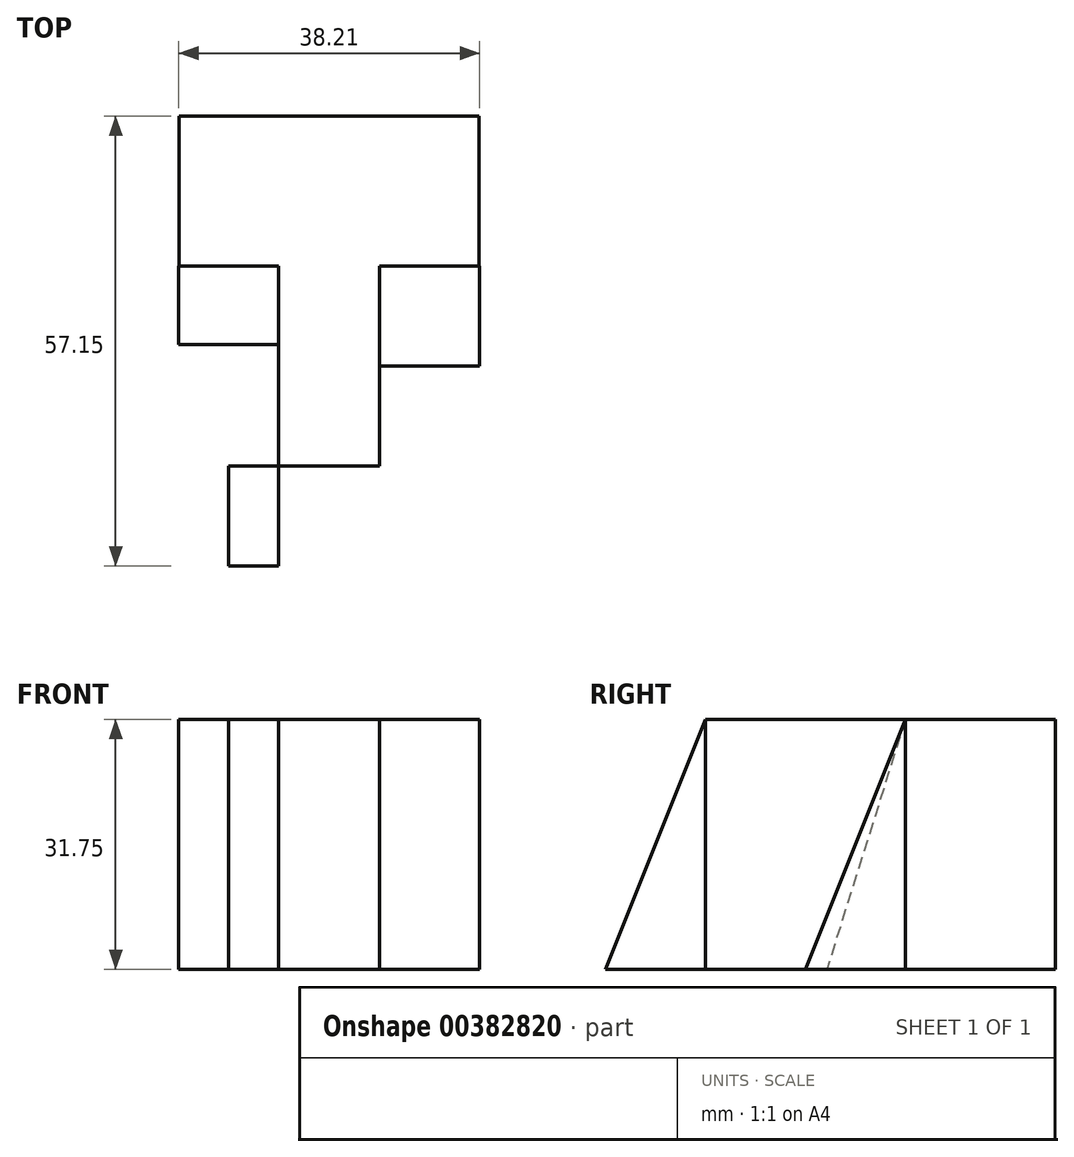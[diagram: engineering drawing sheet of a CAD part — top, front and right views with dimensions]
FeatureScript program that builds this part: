
annotation { "Feature Type Name" : "Feature", "Feature Type Description" : "" }
export const myFeature = defineFeature(function(context is Context, id is Id, definition is map)
    precondition{}
    {
        {
            var Q0;
            Q0=qCreatedBy(makeId("Top.planeOp"),FACE);
            var sketch = newSketch(context, id + "F0", { "sketchPlane" : qUnion([Q0])});
            skLineSegment(sketch, "E0", {"start": v(15.98, 0) * mm, "end": v(15.98, 25.4) * mm});
            skLineSegment(sketch, "E1", {"start": v(15.98, 25.4) * mm, "end": v(3.34, 25.4) * mm});
            skLineSegment(sketch, "E2", {"start": v(3.34, 25.4) * mm, "end": v(3.34, 44.45) * mm});
            skLineSegment(sketch, "E3", {"start": v(3.34, 44.45) * mm, "end": v(41.44, 44.45) * mm});
            skLineSegment(sketch, "E4", {"start": v(41.44, 44.45) * mm, "end": v(41.44, 25.4) * mm});
            skLineSegment(sketch, "E5", {"start": v(41.44, 25.4) * mm, "end": v(28.8, 25.4) * mm});
            skLineSegment(sketch, "E6", {"start": v(28.8, 25.4) * mm, "end": v(28.8, 0) * mm});
            skLineSegment(sketch, "E7", {"start": v(28.8, 0) * mm, "end": v(15.98, 0) * mm});
            skSolve(sketch);
        }
        {
            var Q0;
            Q0 = qSketchRegion(id + "F0", true);
            extrude(context, id + "F1", {"entities" : qUnion([Q0]), "depth" : 31.75 * mm});
        }
        {
            var Q0;
            Q0=makeQuery(id+"F1.opExtrude","SWEPT_FACE",FACE,{"disambiguationData":[OSD([sQuery(id+"F0.wireOp",EDGE,"E0")])]});
            var sketch = newSketch(context, id + "F2", { "sketchPlane" : qUnion([Q0])});
            skLineSegment(sketch, "E8", {"start": v(-25.4, 31.75) * mm, "end": v(-15.4, 0) * mm});
            skLineSegment(sketch, "E9", {"start": v(-15.4, 0) * mm, "end": v(-25.4, 0) * mm});
            skLineSegment(sketch, "E10", {"start": v(-25.4, 0) * mm, "end": v(-25.4, 31.75) * mm});
            skSolve(sketch);
        }
        {
            var Q0;
            Q0=makeQuery(id+"F2.imprint","IMPRINT",FACE,{"disambiguationData":[TD([[makeQuery(id+"F2.imprint","IMPRINT",EDGE,{"derivedFrom":sQuery(id+"F2.wireOp",EDGE,"E8")}),-1.0]])]});
            extrude(context, id + "F3", {"entities" : qUnion([Q0]), "depth" : 12.7 * mm});
        }
        {
            var Q0;
            Q0=makeQuery(id+"F1.opExtrude","SWEPT_FACE",FACE,{"disambiguationData":[OSD([sQuery(id+"F0.wireOp",EDGE,"E6")])]});
            var sketch = newSketch(context, id + "F4", { "sketchPlane" : qUnion([Q0])});
            skLineSegment(sketch, "E11", {"start": v(25.4, 31.75) * mm, "end": v(12.7, 0) * mm});
            skLineSegment(sketch, "E12", {"start": v(12.7, 0) * mm, "end": v(25.4, 0) * mm});
            skLineSegment(sketch, "E13", {"start": v(25.4, 0) * mm, "end": v(25.4, 31.75) * mm});
            skSolve(sketch);
        }
        {
            var Q0;
            Q0 = qSketchRegion(id + "F4", true);
            var Q1;
            Q1=makeQuery(id+"F3.opExtrude","CAP_FACE",FACE,{"disambiguationData":[OSD([sQuery(id+"F2.wireOp",EDGE,"E8"),sQuery(id+"F2.wireOp",EDGE,"E9"),sQuery(id+"F2.wireOp",EDGE,"E10")])],"isStart":false});
            extrude(context, id + "F5", {"entities" : qUnion([Q0, Q1]), "depth" : 12.7 * mm});
        }
        {
            var Q0;
            Q0=makeQuery(id+"F1.opExtrude","SWEPT_FACE",FACE,{"disambiguationData":[OSD([sQuery(id+"F0.wireOp",EDGE,"E0")])]});
            var sketch = newSketch(context, id + "F6", { "sketchPlane" : qUnion([Q0])});
            skLineSegment(sketch, "E14", {"start": v(0, 31.75) * mm, "end": v(12.7, 0) * mm});
            skLineSegment(sketch, "E15", {"start": v(12.7, 0) * mm, "end": v(0, 0) * mm});
            skLineSegment(sketch, "E16", {"start": v(0, 0) * mm, "end": v(0, 31.75) * mm});
            skSolve(sketch);
        }
        {
            var Q0;
            Q0=makeQuery(id+"F6.imprint","IMPRINT",FACE,{"disambiguationData":[TD([[makeQuery(id+"F6.imprint","IMPRINT",EDGE,{"derivedFrom":sQuery(id+"F6.wireOp",EDGE,"E14")}),-1.0]])]});
            extrude(context, id + "F7", {"entities" : qUnion([Q0]), "depth" : 6.35 * mm});
        }
    });
